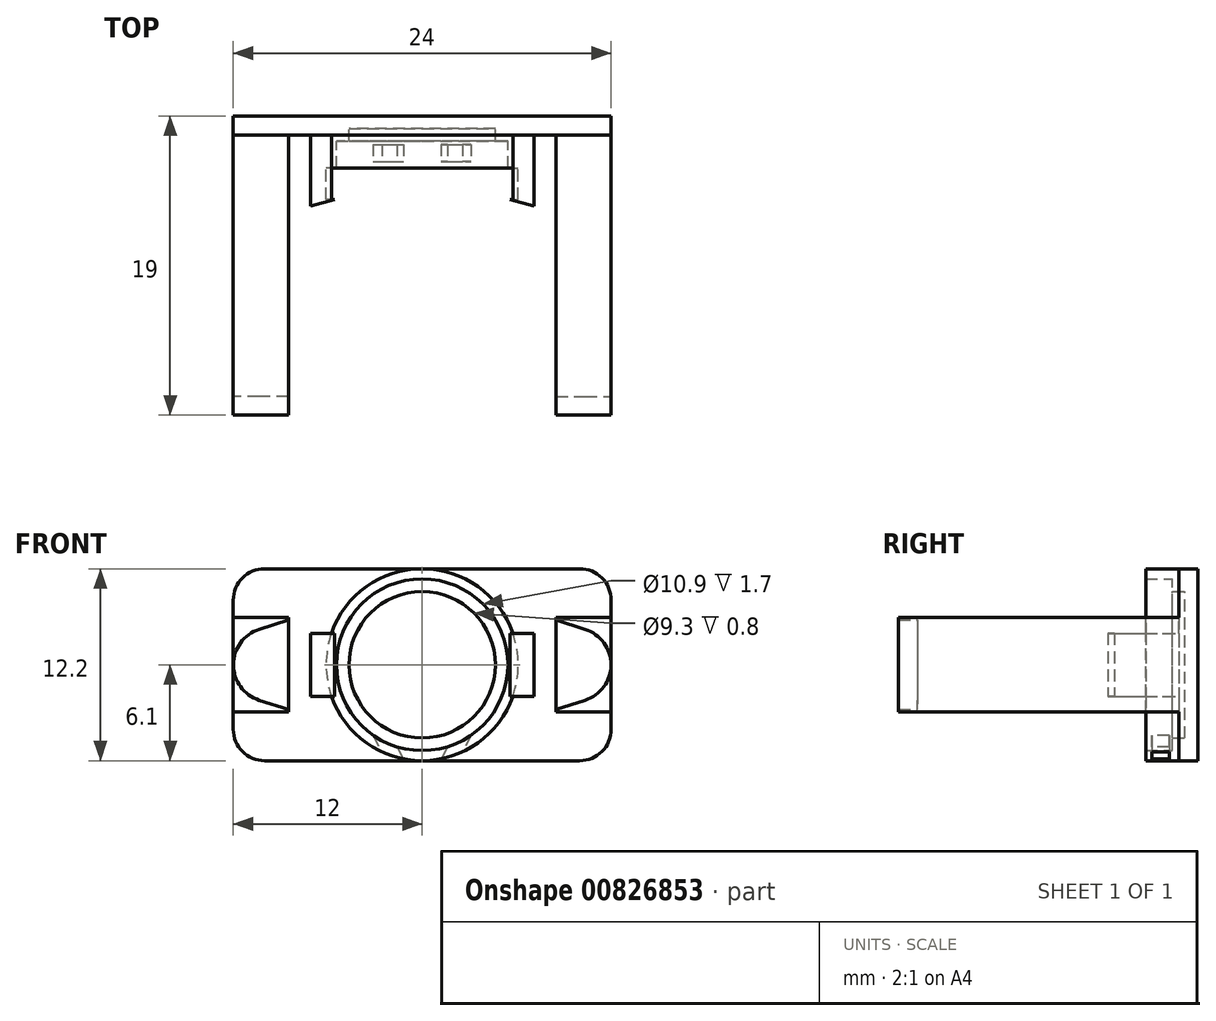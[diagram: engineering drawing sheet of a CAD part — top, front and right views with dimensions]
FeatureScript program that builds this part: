
annotation { "Feature Type Name" : "Feature", "Feature Type Description" : "" }
export const myFeature = defineFeature(function(context is Context, id is Id, definition is map)
    precondition{}
    {
        {
            var Q0;
            Q0=qCreatedBy(makeId("Front.planeOp"),FACE);
            var sketch = newSketch(context, id + "F0", { "sketchPlane" : qUnion([Q0])});
            skCircle(sketch, "E0", {"center": v(0, 0) * mm, "radius": 5 * mm});
            skCircle(sketch, "E1", {"center": v(0, 0) * mm, "radius": 6.1 * mm});
            skSolve(sketch);
        }
        {
            var Q0;
            Q0=makeQuery(id+"F0.imprint","IMPRINT",FACE,{"disambiguationData":[TD([[makeQuery(id+"F0.imprint","IMPRINT",EDGE,{"derivedFrom":sQuery(id+"F0.wireOp",EDGE,"E0")}),-1.0]])]});
            var Q1;
            Q1=makeQuery(id+"F0.imprint","IMPRINT",FACE,{"disambiguationData":[TD([[makeQuery(id+"F0.imprint","IMPRINT",EDGE,{"derivedFrom":sQuery(id+"F0.wireOp",EDGE,"E0")}),1.0]])]});
            extrude(context, id + "F1", {"entities" : qUnion([Q0, Q1]), "depth" : 0.8 * mm, "offsetDistance" : 25 * mm});
        }
        {
            var Q0;
            Q0=makeQuery(id+"F1.opExtrude","CAP_FACE",FACE,{"disambiguationData":[OSD([sQuery(id+"F0.wireOp",EDGE,"E1")])],"isStart":false});
            var sketch = newSketch(context, id + "F2", { "sketchPlane" : qUnion([Q0])});
            skCircle(sketch, "E2", {"center": v(0, 0) * mm, "radius": 5.45 * mm});
            skCircle(sketch, "E3", {"center": v(0, 0) * mm, "radius": 6.1 * mm});
            skSolve(sketch);
        }
        {
            var Q0;
            Q0=makeQuery(id+"F2.imprint","IMPRINT",FACE,{"disambiguationData":[TD([[makeQuery(id+"F2.imprint","IMPRINT",EDGE,{"derivedFrom":sQuery(id+"F2.wireOp",EDGE,"E2")}),-1.0]])]});
            extrude(context, id + "F3", {"entities" : qUnion([Q0]), "operationType" : NewBodyOperationType.ADD, "depth" : 2.5 * mm, "offsetDistance" : 25 * mm});
        }
        {
            var Q0;
            Q0=makeQuery(id+"F1.opExtrude","CAP_FACE",FACE,{"disambiguationData":[OSD([sQuery(id+"F0.wireOp",EDGE,"E1")])],"isStart":false});
            var sketch = newSketch(context, id + "F4", { "sketchPlane" : qUnion([Q0])});
            skCircle(sketch, "E4", {"center": v(0, 0) * mm, "radius": 4.65 * mm});
            skSolve(sketch);
        }
        {
            var Q0;
            Q0=makeQuery(id+"F4.imprint","IMPRINT",FACE,{"disambiguationData":[TD([[makeQuery(id+"F4.imprint","IMPRINT",EDGE,{"derivedFrom":sQuery(id+"F4.wireOp",EDGE,"E4")}),-1.0]])]});
            extrude(context, id + "F5", {"entities" : qUnion([Q0]), "operationType" : NewBodyOperationType.ADD, "depth" : 0.8 * mm, "offsetDistance" : 25 * mm});
        }
        {
            var Q0;
            Q0=makeQuery(id+"F3.opExtrude","CAP_FACE",FACE,{"disambiguationData":[OSD([sQuery(id+"F2.wireOp",EDGE,"E2"),sQuery(id+"F2.wireOp",EDGE,"E3")])],"isStart":false});
            var sketch = newSketch(context, id + "F6", { "sketchPlane" : qUnion([Q0])});
            skLineSegment(sketch, "E5", {"start": v(-1.6, -5.2) * mm, "end": v(-1.2, -5.98) * mm});
            skLineSegment(sketch, "E6", {"start": v(-3.1, -4.48) * mm, "end": v(-2.56, -5.54) * mm});
            skLineSegment(sketch, "E7.MirrorCS", {"start": v(1.6, -5.2) * mm, "end": v(1.2, -5.98) * mm});
            skLineSegment(sketch, "E8.MirrorCS", {"start": v(3.1, -4.48) * mm, "end": v(2.56, -5.54) * mm});
            skCircle(sketch, "E9.0", {"center": v(0, 0) * mm, "radius": 5.45 * mm});
            skSolve(sketch);
        }
        {
            var Q0;
            {var subQ0=sQuery(id+"F6.wireOp",EDGE,"E5");Q0=makeQuery(id+"F6.imprint","IMPRINT",FACE,{"disambiguationData":[TD([[makeQuery(id+"F6.imprint","IMPRINT",EDGE,{"derivedFrom":subQ0}),-1.0]])]});}
            var Q1;
            {var subQ0=sQuery(id+"F6.wireOp",EDGE,"E7.MirrorCS");Q1=makeQuery(id+"F6.imprint","IMPRINT",FACE,{"disambiguationData":[TD([[makeQuery(id+"F6.imprint","IMPRINT",EDGE,{"derivedFrom":subQ0}),1.0]])]});}
            extrude(context, id + "F7", {"entities" : qUnion([Q0, Q1]), "operationType" : NewBodyOperationType.REMOVE, "oppositeDirection" : true, "depth" : 1.5 * mm, "offsetDistance" : 25 * mm});
        }
        {
            var Q0;
            {var subQ0=sQuery(id+"F2.wireOp",EDGE,"E3");var subQ1=sQuery(id+"F2.wireOp",EDGE,"E2");Q0=makeQuery(id+"F7.boolean.opBoolean","SPLIT",FACE,{"disambiguationData":[TD([makeQuery(id+"F7.opExtrude","SWEPT_FACE",FACE,{"disambiguationData":[OSD([sQuery(id+"F6.wireOp",EDGE,"E6")])]})])],"derivedFrom":makeQuery(id+"F3.opExtrude","CAP_FACE",FACE,{"disambiguationData":[OSD([subQ1,subQ0])],"isStart":false})});}
            var sketch = newSketch(context, id + "F8", { "sketchPlane" : qUnion([Q0])});
            skArc(sketch, "E10", {"start": v(-2.56, -5.54) * mm, "mid": v(-1.9, -5.8) * mm, "end": v(-1.2, -5.98) * mm});
            skLineSegment(sketch, "E11", {"start": v(-3.1, -4.48) * mm, "end": v(-2.56, -5.54) * mm});
            skLineSegment(sketch, "E12", {"start": v(-1.6, -5.2) * mm, "end": v(-1.2, -5.98) * mm});
            skLineSegment(sketch, "E13.MirrorCS", {"start": v(3.1, -4.48) * mm, "end": v(2.56, -5.54) * mm});
            skArc(sketch, "E14.MirrorCS", {"start": v(2.56, -5.54) * mm, "mid": v(1.9, -5.8) * mm, "end": v(1.2, -5.98) * mm});
            skLineSegment(sketch, "E15.MirrorCS", {"start": v(1.6, -5.2) * mm, "end": v(1.2, -5.98) * mm});
            skPoint(sketch, "E16.MirrorCS.end.orphan", {"position": v(1.6, -5.2) * mm});
            skPoint(sketch, "E16.MirrorCS.start.orphan", {"position": v(3.1, -4.48) * mm});
            skPoint(sketch, "E17.MirrorCS.end.orphan", {"position": v(-3.1, -4.48) * mm});
            skPoint(sketch, "E17.MirrorCS.start.orphan", {"position": v(-1.6, -5.2) * mm});
            skSolve(sketch);
        }
        {
            var Q0;
            {var subQ0=sQuery(id+"F6.wireOp",EDGE,"E5");Q0=makeQuery(id+"F6.imprint","IMPRINT",FACE,{"disambiguationData":[TD([[makeQuery(id+"F6.imprint","IMPRINT",EDGE,{"derivedFrom":subQ0}),-1.0]])]});}
            var Q1;
            {var subQ0=sQuery(id+"F6.wireOp",EDGE,"E7.MirrorCS");Q1=makeQuery(id+"F6.imprint","IMPRINT",FACE,{"disambiguationData":[TD([[makeQuery(id+"F6.imprint","IMPRINT",EDGE,{"derivedFrom":subQ0}),1.0]])]});}
            extrude(context, id + "F9", {"entities" : qUnion([Q0, Q1]), "operationType" : NewBodyOperationType.ADD, "oppositeDirection" : true, "depth" : 0.4 * mm, "offsetDistance" : 25 * mm});
        }
        {
            var Q0;
            Q0=makeQuery(id+"F1.opExtrude","CAP_FACE",FACE,{"disambiguationData":[OSD([sQuery(id+"F0.wireOp",EDGE,"E1")])],"isStart":true});
            var sketch = newSketch(context, id + "F10", { "sketchPlane" : qUnion([Q0])});
            skLineSegment(sketch, "E18.bottom", {"start": v(-12, -6.1) * mm, "end": v(12, -6.1) * mm});
            skLineSegment(sketch, "E18.top", {"start": v(-12, 6.1) * mm, "end": v(12, 6.1) * mm});
            skLineSegment(sketch, "E18.left", {"start": v(-12, -6.1) * mm, "end": v(-12, 6.1) * mm});
            skLineSegment(sketch, "E18.right", {"start": v(12, -6.1) * mm, "end": v(12, 6.1) * mm});
            skPoint(sketch, "E18.middle", {"position": v(0, 0) * mm});
            skSolve(sketch);
        }
        {
            var Q0;
            {var subQ0=sQuery(id+"F10.wireOp",EDGE,"E18.right");Q0=makeQuery(id+"F10.imprint","IMPRINT",FACE,{"disambiguationData":[TD([[makeQuery(id+"F10.imprint","IMPRINT",EDGE,{"derivedFrom":subQ0}),1.0]])]});}
            var Q1;
            {var subQ0=sQuery(id+"F10.wireOp",EDGE,"E18.left");Q1=makeQuery(id+"F10.imprint","IMPRINT",FACE,{"disambiguationData":[TD([[makeQuery(id+"F10.imprint","IMPRINT",EDGE,{"derivedFrom":subQ0}),-1.0]])]});}
            extrude(context, id + "F11", {"entities" : qUnion([Q0, Q1]), "operationType" : NewBodyOperationType.ADD, "oppositeDirection" : true, "depth" : 1.2 * mm, "offsetDistance" : 25 * mm});
        }
        {
            var Q0;
            Q0=makeQuery(id+"F11.opExtrude","SWEPT_EDGE",EDGE,{"disambiguationData":[OSD([sQuery(id+"F10.wireOp",EDGE,"E18.bottom"),sQuery(id+"F10.wireOp",EDGE,"E18.right")])]});
            var Q1;
            Q1=makeQuery(id+"F11.opExtrude","SWEPT_EDGE",EDGE,{"disambiguationData":[OSD([sQuery(id+"F10.wireOp",EDGE,"E18.bottom"),sQuery(id+"F10.wireOp",EDGE,"E18.left")])]});
            var Q2;
            Q2=makeQuery(id+"F11.opExtrude","SWEPT_EDGE",EDGE,{"disambiguationData":[OSD([sQuery(id+"F10.wireOp",EDGE,"E18.top"),sQuery(id+"F10.wireOp",EDGE,"E18.left")])]});
            var Q3;
            Q3=makeQuery(id+"F11.opExtrude","SWEPT_EDGE",EDGE,{"disambiguationData":[OSD([sQuery(id+"F10.wireOp",EDGE,"E18.top"),sQuery(id+"F10.wireOp",EDGE,"E18.right")])]});
            fillet(context, id + "F12", {"entities" : qUnion([Q0, Q1, Q2, Q3]), "radius" : 2 * mm, "tangentPropagation" : true, "allowEdgeOverflow" : false});
        }
        {
            var Q0;
            Q0=makeQuery(id+"F11.opExtrude","CAP_FACE",FACE,{"disambiguationData":[OSD([sQuery(id+"F0.wireOp",EDGE,"E1"),sQuery(id+"F10.wireOp",EDGE,"E18.bottom"),sQuery(id+"F10.wireOp",EDGE,"E18.top"),sQuery(id+"F10.wireOp",EDGE,"E18.right")])],"isStart":false});
            var sketch = newSketch(context, id + "F13", { "sketchPlane" : qUnion([Q0])});
            skLineSegment(sketch, "E19", {"start": v(-12, 3) * mm, "end": v(-8.5, 3) * mm});
            skLineSegment(sketch, "E20", {"start": v(-8.5, 3) * mm, "end": v(-8.5, -3) * mm});
            skLineSegment(sketch, "E21", {"start": v(-8.5, -3) * mm, "end": v(-12, -3) * mm});
            skLineSegment(sketch, "E22", {"start": v(-7.1, 2) * mm, "end": v(-7.1, -2) * mm});
            skLineSegment(sketch, "E23", {"start": v(-7.1, -2) * mm, "end": v(-5.76, -2) * mm});
            skLineSegment(sketch, "E24", {"start": v(-7.1, 2) * mm, "end": v(-5.76, 2) * mm});
            skSolve(sketch);
        }
        {
            var Q0;
            {var subQ0=sQuery(id+"F13.wireOp",EDGE,"E19");Q0=makeQuery(id+"F13.imprint","IMPRINT",FACE,{"disambiguationData":[TD([[makeQuery(id+"F13.imprint","IMPRINT",EDGE,{"derivedFrom":subQ0}),-1.0]])]});}
            extrude(context, id + "F14", {"entities" : qUnion([Q0]), "operationType" : NewBodyOperationType.ADD, "depth" : 16.6 * mm, "offsetDistance" : 25 * mm});
        }
        {
            var Q0;
            Q0=makeQuery(id+"F11.opExtrude","CAP_FACE",FACE,{"disambiguationData":[OSD([sQuery(id+"F0.wireOp",EDGE,"E1"),sQuery(id+"F10.wireOp",EDGE,"E18.bottom"),sQuery(id+"F10.wireOp",EDGE,"E18.top"),sQuery(id+"F10.wireOp",EDGE,"E18.left")])],"isStart":false});
            var sketch = newSketch(context, id + "F15", { "sketchPlane" : qUnion([Q0])});
            skLineSegment(sketch, "E25", {"start": v(12, 3) * mm, "end": v(8.5, 3) * mm});
            skLineSegment(sketch, "E26", {"start": v(8.5, 3) * mm, "end": v(8.5, -3) * mm});
            skLineSegment(sketch, "E27", {"start": v(8.5, -3) * mm, "end": v(12, -3) * mm});
            skLineSegment(sketch, "E28", {"start": v(7.1, 2) * mm, "end": v(7.1, -2) * mm});
            skLineSegment(sketch, "E29", {"start": v(7.1, -2) * mm, "end": v(5.76, -2) * mm});
            skLineSegment(sketch, "E30", {"start": v(7.1, 2) * mm, "end": v(5.76, 2) * mm});
            skSolve(sketch);
        }
        {
            var Q0;
            {var subQ0=sQuery(id+"F15.wireOp",EDGE,"E25");Q0=makeQuery(id+"F15.imprint","IMPRINT",FACE,{"disambiguationData":[TD([[makeQuery(id+"F15.imprint","IMPRINT",EDGE,{"derivedFrom":subQ0}),1.0]])]});}
            extrude(context, id + "F16", {"entities" : qUnion([Q0]), "operationType" : NewBodyOperationType.ADD, "depth" : 16.6 * mm, "offsetDistance" : 25 * mm});
        }
        {
            var Q0;
            Q0=makeQuery(id+"F15.imprint","IMPRINT",FACE,{"disambiguationData":[TD([[makeQuery(id+"F15.imprint","IMPRINT",EDGE,{"derivedFrom":sQuery(id+"F15.wireOp",EDGE,"E28")}),-1.0]])]});
            var Q1;
            Q1=makeQuery(id+"F13.imprint","IMPRINT",FACE,{"disambiguationData":[TD([[makeQuery(id+"F13.imprint","IMPRINT",EDGE,{"derivedFrom":sQuery(id+"F13.wireOp",EDGE,"E22")}),1.0]])]});
            extrude(context, id + "F17", {"entities" : qUnion([Q0, Q1]), "operationType" : NewBodyOperationType.ADD, "depth" : 4.1 * mm, "offsetDistance" : 25 * mm});
        }
        {
            var Q0;
            Q0=makeQuery(id+"F17.opExtrude","SWEPT_FACE",FACE,{"disambiguationData":[OSD([sQuery(id+"F13.wireOp",EDGE,"E23")])]});
            var sketch = newSketch(context, id + "F18", { "sketchPlane" : qUnion([Q0])});
            skLineSegment(sketch, "E31", {"start": v(-7.1, 5.3) * mm, "end": v(-7.1, 5.7) * mm});
            skLineSegment(sketch, "E32", {"start": v(-5.76, 5.3) * mm, "end": v(-5.66, 5.3) * mm});
            skLineSegment(sketch, "E33", {"start": v(-5.66, 5.3) * mm, "end": v(-7.1, 5.7) * mm});
            skSolve(sketch);
        }
        {
            var Q0;
            Q0=makeQuery(id+"F18.imprint","IMPRINT",FACE,{"disambiguationData":[TD([[makeQuery(id+"F18.imprint","IMPRINT",EDGE,{"derivedFrom":sQuery(id+"F18.wireOp",EDGE,"E31")}),-1.0]])]});
            extrude(context, id + "F19", {"entities" : qUnion([Q0]), "operationType" : NewBodyOperationType.ADD, "oppositeDirection" : true, "depth" : 4 * mm, "offsetDistance" : 25 * mm});
        }
        {
            var Q0;
            Q0=makeQuery(id+"F17.opExtrude","SWEPT_FACE",FACE,{"disambiguationData":[OSD([sQuery(id+"F15.wireOp",EDGE,"E29")])]});
            var sketch = newSketch(context, id + "F20", { "sketchPlane" : qUnion([Q0])});
            skLineSegment(sketch, "E34", {"start": v(7.1, 5.3) * mm, "end": v(7.1, 5.7) * mm});
            skLineSegment(sketch, "E35", {"start": v(5.76, 5.3) * mm, "end": v(5.66, 5.3) * mm});
            skLineSegment(sketch, "E36", {"start": v(5.66, 5.3) * mm, "end": v(7.1, 5.7) * mm});
            skSolve(sketch);
        }
        {
            var Q0;
            Q0=makeQuery(id+"F20.imprint","IMPRINT",FACE,{"disambiguationData":[TD([[makeQuery(id+"F20.imprint","IMPRINT",EDGE,{"derivedFrom":sQuery(id+"F20.wireOp",EDGE,"E34")}),1.0]])]});
            extrude(context, id + "F21", {"entities" : qUnion([Q0]), "operationType" : NewBodyOperationType.ADD, "oppositeDirection" : true, "depth" : 4 * mm, "offsetDistance" : 25 * mm});
        }
        {
            var Q0;
            {var subQ0=sQuery(id+"F13.wireOp",EDGE,"E23");Q0=makeQuery(id+"F19.boolean.opBoolean","MERGE",FACE,{"derivedFrom":[makeQuery(id+"F17.opExtrude","SWEPT_FACE",FACE,{"disambiguationData":[OSD([subQ0])]}),makeQuery(id+"F19.opExtrude","CAP_FACE",FACE,{"disambiguationData":[OSD([subQ0,sQuery(id+"F18.wireOp",EDGE,"E31"),sQuery(id+"F18.wireOp",EDGE,"scbSYdZa-IKE8-HjIA-PmpS-5iz6sRiiHXsu")])],"isStart":true})]});}
            var sketch = newSketch(context, id + "F22", { "sketchPlane" : qUnion([Q0])});
            skLineSegment(sketch, "E37", {"start": v(-5.76, 5.3) * mm, "end": v(-5.56, 5.3) * mm});
            skLineSegment(sketch, "E38", {"start": v(-5.56, 5.3) * mm, "end": v(-7.1, 5.7) * mm});
            skSolve(sketch);
        }
        {
            var Q0;
            Q0=makeQuery(id+"F22.imprint","IMPRINT",FACE,{"disambiguationData":[TD([[makeQuery(id+"F22.imprint","IMPRINT",EDGE,{"derivedFrom":sQuery(id+"F22.wireOp",EDGE,"E37")}),1.0]])]});
            extrude(context, id + "F23", {"entities" : qUnion([Q0]), "operationType" : NewBodyOperationType.ADD, "oppositeDirection" : true, "depth" : 4 * mm, "offsetDistance" : 25 * mm});
        }
        {
            var Q0;
            {var subQ0=sQuery(id+"F15.wireOp",EDGE,"E29");Q0=makeQuery(id+"F21.boolean.opBoolean","MERGE",FACE,{"derivedFrom":[makeQuery(id+"F17.opExtrude","SWEPT_FACE",FACE,{"disambiguationData":[OSD([subQ0])]}),makeQuery(id+"F21.opExtrude","CAP_FACE",FACE,{"disambiguationData":[OSD([subQ0,sQuery(id+"F20.wireOp",EDGE,"E34"),sQuery(id+"F20.wireOp",EDGE,"OUZQXp2e-nWsZ-sgYy-KXVV-Yu3MqT17kAb9")])],"isStart":true})]});}
            var sketch = newSketch(context, id + "F24", { "sketchPlane" : qUnion([Q0])});
            skLineSegment(sketch, "E39", {"start": v(5.76, 5.3) * mm, "end": v(5.56, 5.3) * mm});
            skLineSegment(sketch, "E40", {"start": v(5.56, 5.3) * mm, "end": v(7.1, 5.7) * mm});
            skSolve(sketch);
        }
        {
            var Q0;
            Q0=makeQuery(id+"F24.imprint","IMPRINT",FACE,{"disambiguationData":[TD([[makeQuery(id+"F24.imprint","IMPRINT",EDGE,{"derivedFrom":sQuery(id+"F24.wireOp",EDGE,"E39")}),-1.0]])]});
            extrude(context, id + "F25", {"entities" : qUnion([Q0]), "operationType" : NewBodyOperationType.ADD, "oppositeDirection" : true, "depth" : 4 * mm, "offsetDistance" : 25 * mm});
        }
        {
            var Q0;
            Q0=makeQuery(id+"F16.opExtrude","CAP_FACE",FACE,{"disambiguationData":[OSD([sQuery(id+"F10.wireOp",EDGE,"E18.left"),sQuery(id+"F15.wireOp",EDGE,"E25"),sQuery(id+"F15.wireOp",EDGE,"E26"),sQuery(id+"F15.wireOp",EDGE,"E27")])],"isStart":false});
            var sketch = newSketch(context, id + "F26", { "sketchPlane" : qUnion([Q0])});
            skLineSegment(sketch, "E41", {"start": v(8.5, 2.85) * mm, "end": v(10.35, 2.25) * mm});
            skArc(sketch, "E42", {"start": v(10.35, -2.25) * mm, "mid": v(11.99, 0) * mm, "end": v(10.35, 2.25) * mm});
            skLineSegment(sketch, "E43.MirrorCS", {"start": v(8.5, -2.85) * mm, "end": v(10.35, -2.25) * mm});
            skSolve(sketch);
        }
        {
            var Q0;
            {var subQ2=sQuery(id+"F26.wireOp",EDGE,"E41");Q0=makeQuery(id+"F26.imprint","IMPRINT",FACE,{"disambiguationData":[TD([[makeQuery(id+"F26.imprint","IMPRINT",EDGE,{"derivedFrom":subQ2}),1.0]])]});}
            extrude(context, id + "F27", {"entities" : qUnion([Q0]), "operationType" : NewBodyOperationType.ADD, "depth" : 1.2 * mm, "offsetDistance" : 25 * mm});
        }
        {
            var Q0;
            Q0=makeQuery(id+"F14.opExtrude","CAP_FACE",FACE,{"disambiguationData":[OSD([sQuery(id+"F10.wireOp",EDGE,"E18.right"),sQuery(id+"F13.wireOp",EDGE,"E19"),sQuery(id+"F13.wireOp",EDGE,"E20"),sQuery(id+"F13.wireOp",EDGE,"E21")])],"isStart":false});
            var sketch = newSketch(context, id + "F28", { "sketchPlane" : qUnion([Q0])});
            skLineSegment(sketch, "E44", {"start": v(-8.5, 2.85) * mm, "end": v(-10.35, 2.25) * mm});
            skLineSegment(sketch, "E45.MirrorCS", {"start": v(-8.5, -2.85) * mm, "end": v(-10.35, -2.25) * mm});
            skArc(sketch, "E46", {"start": v(-10.35, 2.25) * mm, "mid": v(-12, 0) * mm, "end": v(-10.35, -2.25) * mm});
            skSolve(sketch);
        }
        {
            var Q0;
            {var subQ2=sQuery(id+"F28.wireOp",EDGE,"E44");Q0=makeQuery(id+"F28.imprint","IMPRINT",FACE,{"disambiguationData":[TD([[makeQuery(id+"F28.imprint","IMPRINT",EDGE,{"derivedFrom":subQ2}),-1.0]])]});}
            extrude(context, id + "F29", {"entities" : qUnion([Q0]), "operationType" : NewBodyOperationType.ADD, "depth" : 1.2 * mm, "offsetDistance" : 25 * mm});
        }
    });
